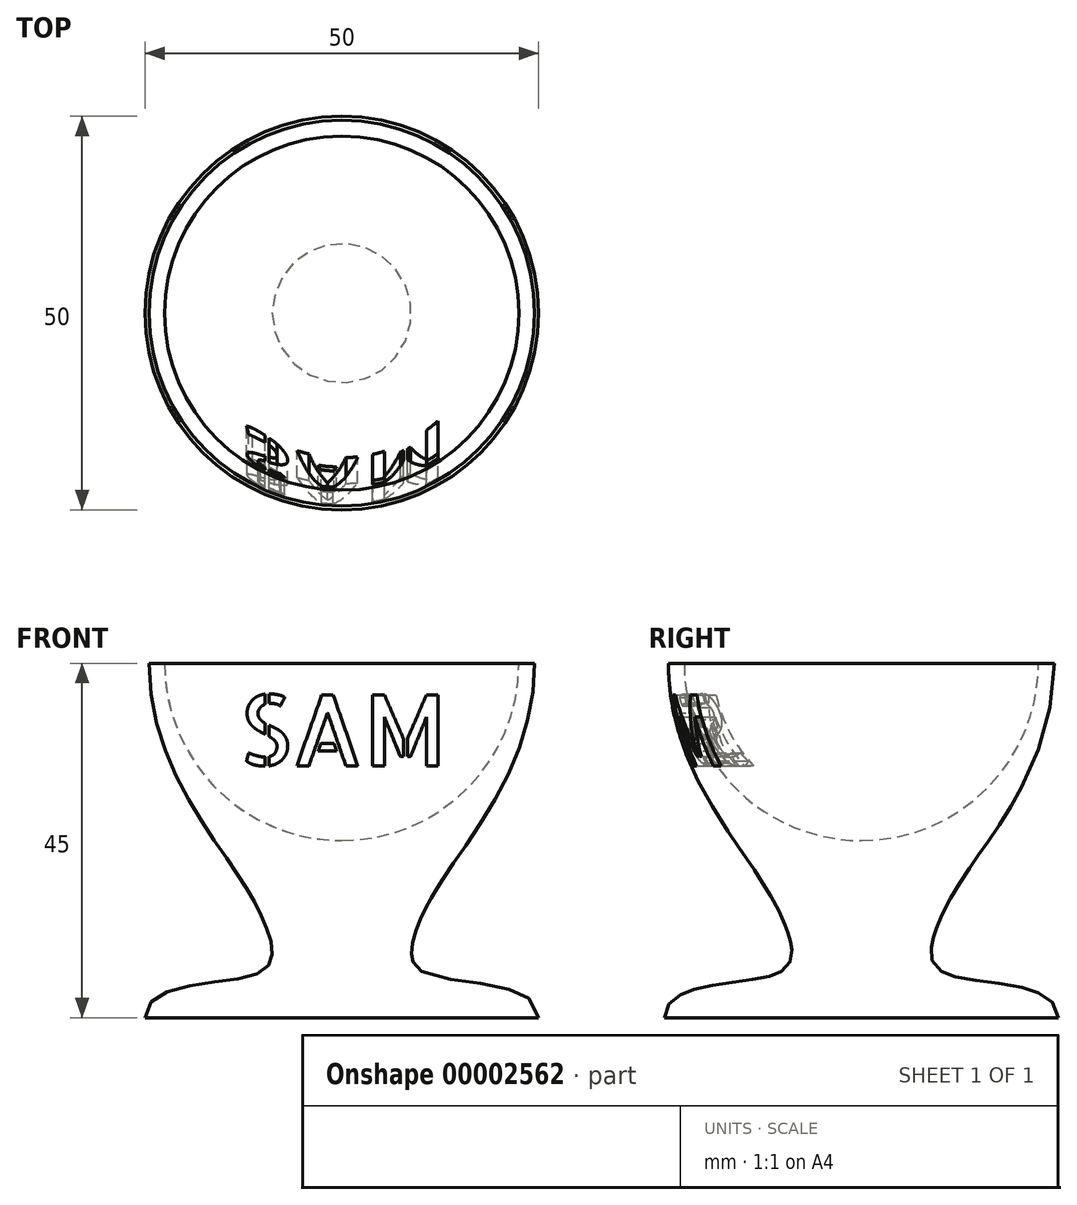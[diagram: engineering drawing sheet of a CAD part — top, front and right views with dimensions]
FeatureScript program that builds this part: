
annotation { "Feature Type Name" : "Feature", "Feature Type Description" : "" }
export const myFeature = defineFeature(function(context is Context, id is Id, definition is map)
    precondition{}
    {
        {
            var Q0;
            Q0=qCreatedBy(makeId("Front.planeOp"),FACE);
            var sketch = newSketch(context, id + "F0", { "sketchPlane" : qUnion([Q0])});
            skLineSegment(sketch, "E0", {"start": v(-25, 0) * mm, "end": v(0, 0) * mm});
            skLineSegment(sketch, "E1", {"start": v(0, 0) * mm, "end": v(0, 45) * mm});
            skCircle(sketch, "E2", {"center": v(0, 45) * mm, "radius": 22.5 * mm});
            skLineSegment(sketch, "E3", {"start": v(-22.5, 45) * mm, "end": v(-24.5, 45) * mm});
            skFitSpline(sketch, "E4", {"points": [v(-24.5, 45) * mm, v(-14.46, 20.03) * mm, v(-9.46, 11.14) * mm, v(-10.35, 5.77) * mm, v(-25, 0) * mm], "startDerivative": vector(0.05, -93.93) * mm, "endDerivative": vector(-0.5, -57.27) * mm});
            skSolve(sketch);
        }
        {
            var Q0;
            {var subQ4=sQuery(id+"F0.wireOp",EDGE,"E0");Q0=makeQuery(id+"F0.imprint","IMPRINT",FACE,{"disambiguationData":[TD([[makeQuery(id+"F0.imprint","IMPRINT",EDGE,{"derivedFrom":subQ4}),1.0]])]});}
            var Q1;
            Q1=sQuery(id+"F0.wireOp",EDGE,"E1");
            revolve(context, id + "F1", {"entities" : qUnion([Q0]), "axis" : qUnion([Q1]), "revolveType" : RevolveType.FULL});
        }
        {
            var Q0;
            Q0=qCreatedBy(makeId("Front.planeOp"),FACE);
            var sketch = newSketch(context, id + "F2", { "sketchPlane" : qUnion([Q0])});
            skText(sketch, "E5", { "text": "SAM", "fontName": "AllertaStencil-Regular.ttf"});
            skLineSegment(sketch, "E6", {"start": v(0, 32) * mm, "end": v(0, 0) * mm, "construction": true});
            const initialGuessF2  = {"E5": [-0.01308, 0.032, 1, 0, 0.009]};
            skSetInitialGuess(sketch, initialGuessF2);
            skSolve(sketch);
        }
        {
            var Q0;
            Q0 = qSketchRegion(id + "F2", true);
            extrude(context, id + "F3", {"entities" : qUnion([Q0]), "operationType" : NewBodyOperationType.REMOVE, "depth" : 28.2 * mm});
        }
    });
